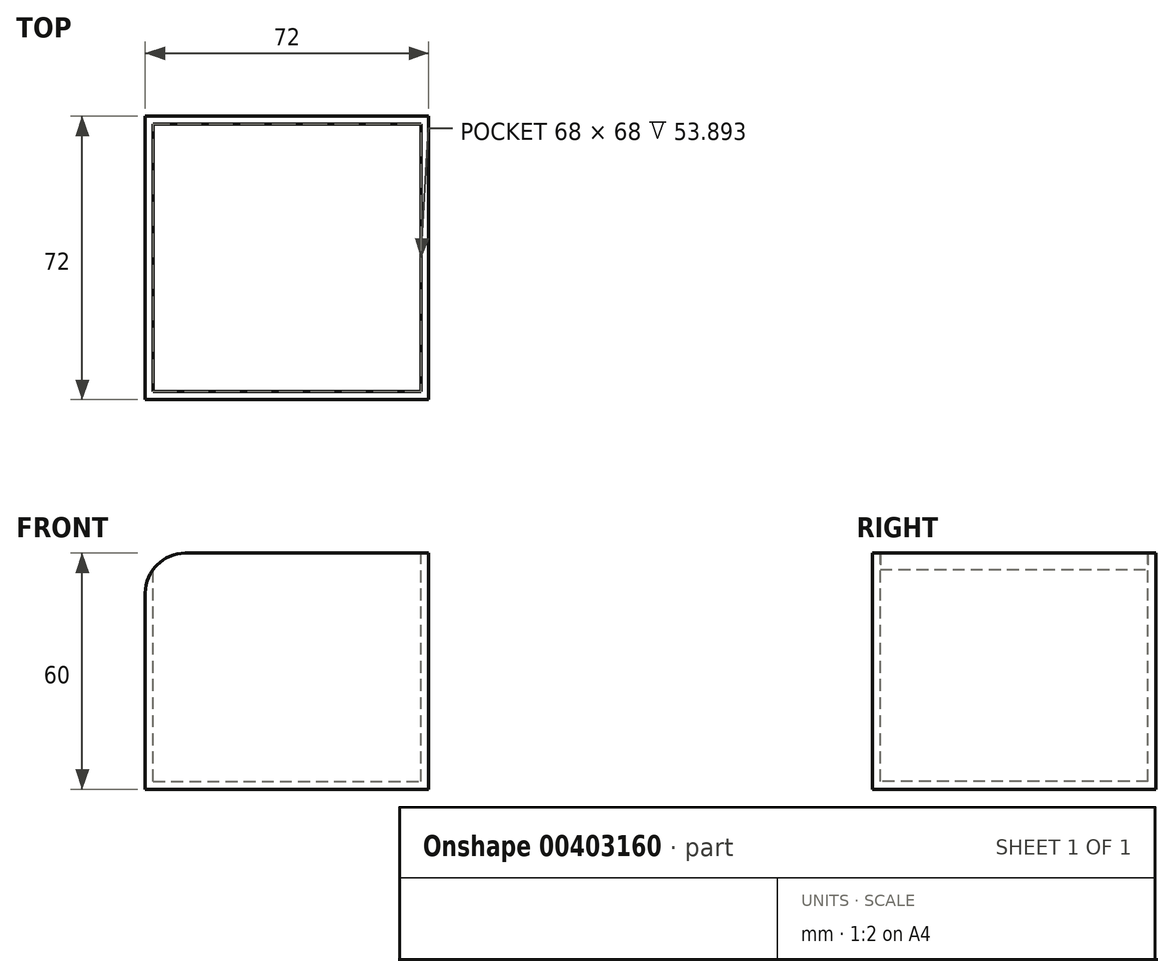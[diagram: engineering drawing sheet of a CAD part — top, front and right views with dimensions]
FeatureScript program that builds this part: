
annotation { "Feature Type Name" : "Feature", "Feature Type Description" : "" }
export const myFeature = defineFeature(function(context is Context, id is Id, definition is map)
    precondition{}
    {
        {
            var Q0;
            Q0=qCreatedBy(makeId("Top.planeOp"),FACE);
            var sketch = newSketch(context, id + "F0", { "sketchPlane" : qUnion([Q0])});
            skLineSegment(sketch, "E0.bottom", {"start": v(-11.32, 57.65) * mm, "end": v(60.68, 57.65) * mm});
            skLineSegment(sketch, "E0.top", {"start": v(-11.32, -14.35) * mm, "end": v(60.68, -14.35) * mm});
            skLineSegment(sketch, "E0.left", {"start": v(-11.32, 57.65) * mm, "end": v(-11.32, -14.35) * mm});
            skLineSegment(sketch, "E0.right", {"start": v(60.68, 57.65) * mm, "end": v(60.68, -14.35) * mm});
            skSolve(sketch);
        }
        {
            var Q0;
            Q0=makeQuery(id+"F0.imprint","IMPRINT",FACE,{"disambiguationData":[TD([[makeQuery(id+"F0.imprint","IMPRINT",EDGE,{"derivedFrom":sQuery(id+"F0.wireOp",EDGE,"E0.bottom")}),-1.0]])]});
            extrude(context, id + "F1", {"entities" : qUnion([Q0]), "depth" : 60 * mm});
        }
        {
            var Q0;
            Q0=makeQuery(id+"F1.opExtrude","CAP_FACE",FACE,{"disambiguationData":[OSD([sQuery(id+"F0.wireOp",EDGE,"E0.bottom"),sQuery(id+"F0.wireOp",EDGE,"E0.top"),sQuery(id+"F0.wireOp",EDGE,"E0.left"),sQuery(id+"F0.wireOp",EDGE,"E0.right")])],"isStart":false});
            var sketch = newSketch(context, id + "F2", { "sketchPlane" : qUnion([Q0])});
            skLineSegment(sketch, "E1.bottom", {"start": v(-9.32, 55.65) * mm, "end": v(58.68, 55.65) * mm});
            skLineSegment(sketch, "E1.top", {"start": v(-9.32, -12.35) * mm, "end": v(58.68, -12.35) * mm});
            skLineSegment(sketch, "E1.left", {"start": v(-9.32, 55.65) * mm, "end": v(-9.32, -12.35) * mm});
            skLineSegment(sketch, "E1.right", {"start": v(58.68, 55.65) * mm, "end": v(58.68, -12.35) * mm});
            skSolve(sketch);
        }
        {
            var Q0;
            Q0=makeQuery(id+"F2.imprint","IMPRINT",FACE,{"disambiguationData":[TD([[makeQuery(id+"F2.imprint","IMPRINT",EDGE,{"derivedFrom":sQuery(id+"F2.wireOp",EDGE,"E1.bottom")}),-1.0]])]});
            extrude(context, id + "F3", {"entities" : qUnion([Q0]), "operationType" : NewBodyOperationType.REMOVE, "oppositeDirection" : true, "depth" : 58 * mm});
        }
        {
            var Q0;
            Q0=makeQuery(id+"F1.opExtrude","CAP_EDGE",EDGE,{"disambiguationData":[OSD([sQuery(id+"F0.wireOp",EDGE,"E0.left")])],"isStart":false});
            fillet(context, id + "F4", {"entities" : qUnion([Q0]), "radius" : 10.16 * mm, "tangentPropagation" : true, "allowEdgeOverflow" : false});
        }
    });
